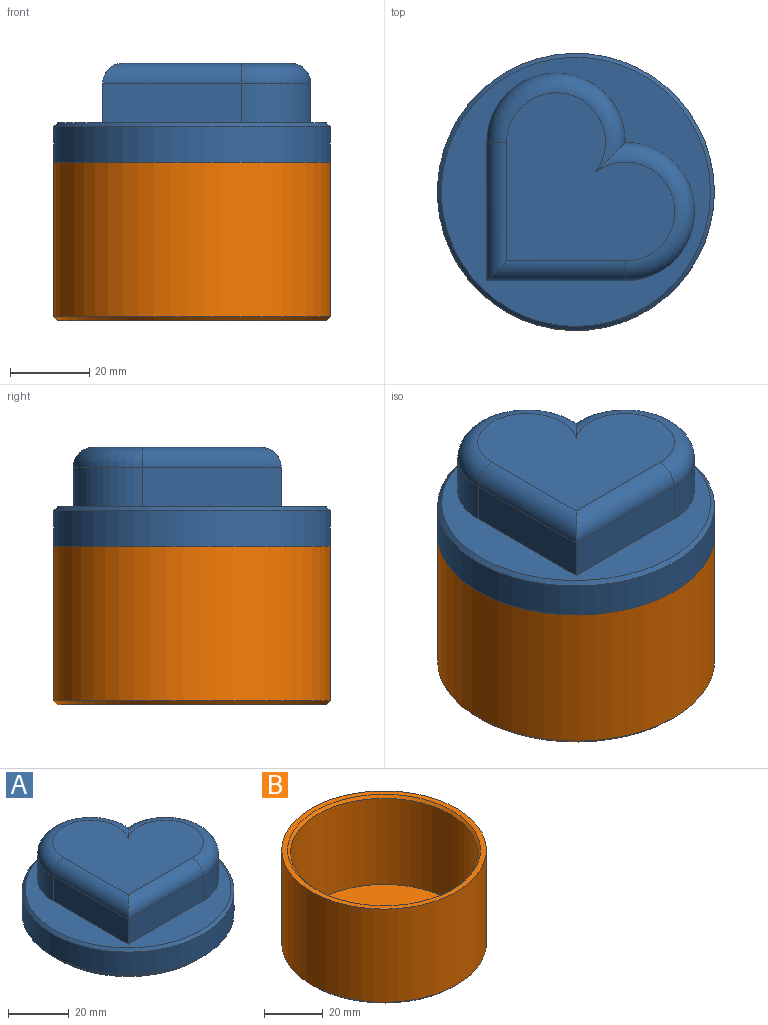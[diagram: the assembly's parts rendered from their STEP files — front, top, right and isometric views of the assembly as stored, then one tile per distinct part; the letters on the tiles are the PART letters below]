
ASSEMBLY  parts=2 mates=1
PART A: 15 faces, bbox 70x70x28 mm
  f0: cylinder r=17.5mm len=35mm, axis (0,0,1), area 549.8mm2, adj f1,f3,f6,f10
  f1: cylinder r=17.5mm len=35mm, axis (0,0,1), area 549.8mm2, adj f0,f2,f6,f9
  f2: plane 35x10mm, normal (-1,0,0), area 350mm2, adj f1,f3,f6,f7
  f3: plane 35x10mm, normal (0,-1,0), area 350mm2, adj f0,f2,f6,f8
  f4: plane 42.5x42.5mm, normal (0,0,1), area 1360.2mm2, adj f7,f8,f9,f10
  f5: cylinder r=35mm len=70mm, axis (0,0,1), area 1979.2mm2, adj f11,f13
  f6: plane 68x68mm, normal (0,0,1), area 1444.6mm2, adj f0,f1,f2,f3,f11
  f7: cylinder r=5mm len=35mm, axis (0,-1,0), area 260.6mm2, adj f2,f4,f8,f9
  f8: cylinder r=5mm len=35mm, axis (1,0,0), area 260.6mm2, adj f3,f4,f7,f10
  f9: torus R=12.5mm, axis (0,0,1), area 404.2mm2, adj f1,f4,f7,f10
  f10: torus R=12.5mm, axis (0,0,1), area 404.2mm2, adj f0,f4,f8,f9
  f11: cone r=34mm half-angle=45deg, axis (0,0,-1), area 306.6mm2, adj f5,f6
  f12: cylinder r=32mm len=64mm, axis (0,0,1), area 603.2mm2, adj f13,f14
  f13: plane 70x70mm, normal (0,0,-1), area 631.5mm2, adj f5,f12
  f14: plane 64x64mm, normal (0,0,-1), area 3217mm2, adj f12
PART B: 7 faces, bbox 70x70x40 mm
  f0: cylinder r=32mm len=64mm, axis (0,0,1), area 7238.2mm2, adj f4,f6
  f1: cylinder r=35mm len=70mm, axis (0,0,1), area 8576.5mm2, adj f2,f5
  f2: plane 70x70mm, normal (0,0,1), area 427.3mm2, adj f1,f6
  f3: plane 68x68mm, normal (0,0,-1), area 3631.7mm2, adj f5
  f4: plane 64x64mm, normal (0,0,1), area 3217mm2, adj f0
  f5: cone r=35mm half-angle=45deg, axis (0,0,1), area 306.6mm2, adj f1,f3
  f6: cone r=32mm half-angle=45deg, axis (0,0,1), area 288.8mm2, adj f0,f2
PLACE A t=(0,0,37)mm
PLACE B at identity
MATE fastened A.f5 <-> B.f1  axis (0,0,-1) through (0,0,40)mm
